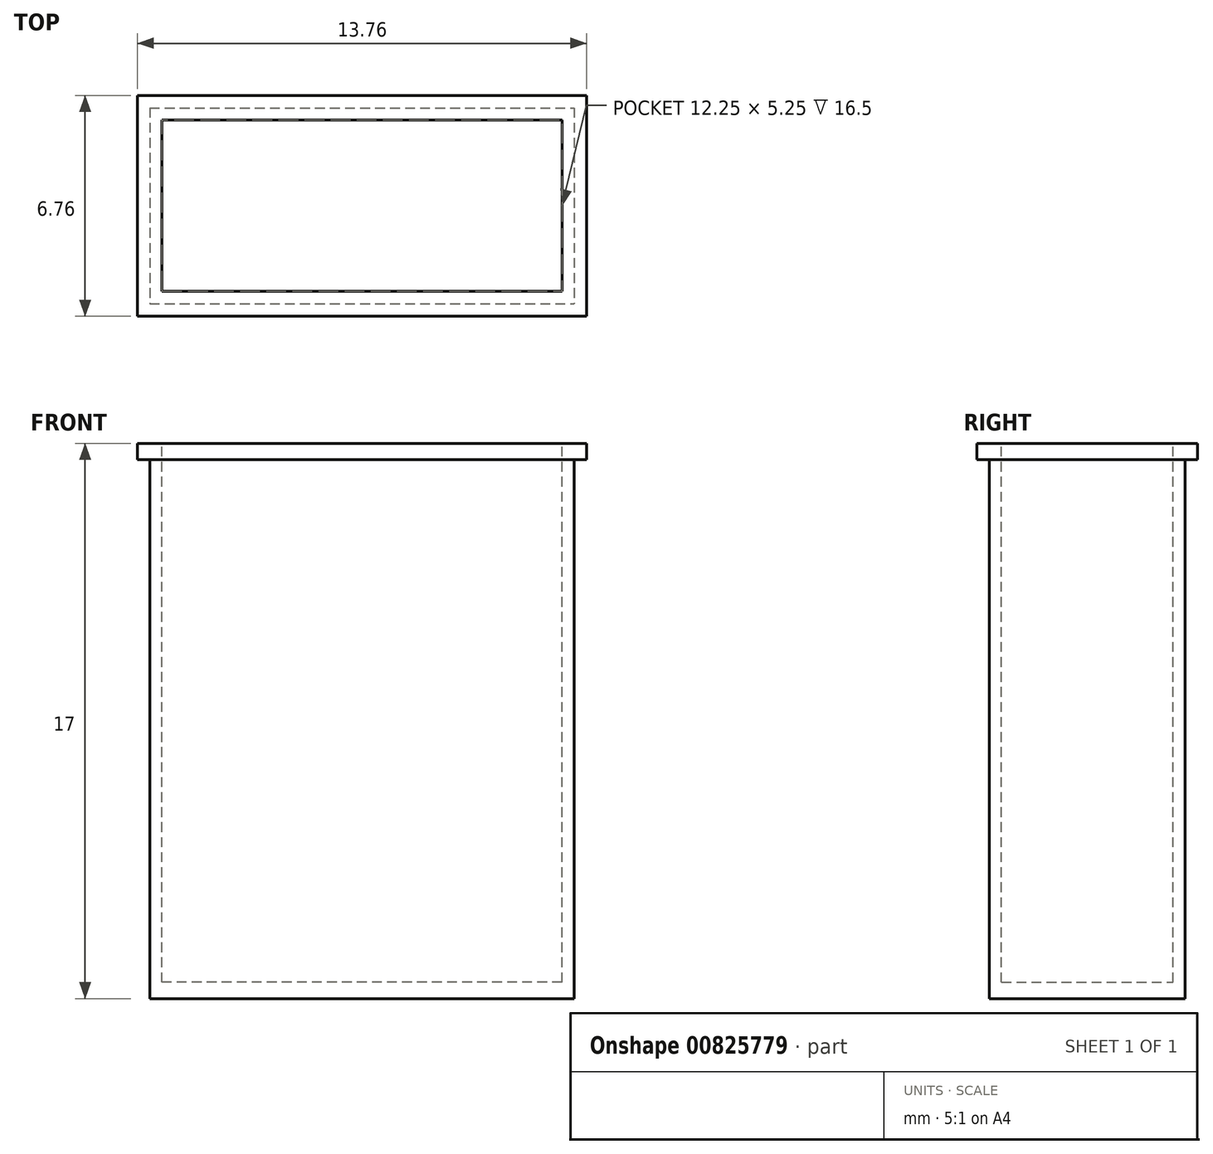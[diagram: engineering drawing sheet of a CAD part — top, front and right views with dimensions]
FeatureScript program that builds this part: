
annotation { "Feature Type Name" : "Feature", "Feature Type Description" : "" }
export const myFeature = defineFeature(function(context is Context, id is Id, definition is map)
    precondition{}
    {
        {
            var Q0;
            Q0=qCreatedBy(makeId("Top.planeOp"),FACE);
            var sketch = newSketch(context, id + "F0", { "sketchPlane" : qUnion([Q0])});
            skLineSegment(sketch, "E0.bottom", {"start": v(-6.5, 3) * mm, "end": v(6.5, 3) * mm});
            skLineSegment(sketch, "E0.top", {"start": v(-6.5, -3) * mm, "end": v(6.5, -3) * mm});
            skLineSegment(sketch, "E0.left", {"start": v(-6.5, 3) * mm, "end": v(-6.5, -3) * mm});
            skLineSegment(sketch, "E0.right", {"start": v(6.5, 3) * mm, "end": v(6.5, -3) * mm});
            skLineSegment(sketch, "E1", {"start": v(0, 0) * mm, "end": v(-6.5, 0) * mm, "construction": true});
            skLineSegment(sketch, "E2", {"start": v(0, 0) * mm, "end": v(0, 3) * mm, "construction": true});
            skLineSegment(sketch, "E3", {"start": v(0, 0) * mm, "end": v(6.5, 0) * mm, "construction": true});
            skLineSegment(sketch, "E4", {"start": v(0, 0) * mm, "end": v(0, -3) * mm, "construction": true});
            skSolve(sketch);
        }
        {
            var Q0;
            Q0=makeQuery(id+"F0.imprint","IMPRINT",FACE,{"disambiguationData":[TD([[makeQuery(id+"F0.imprint","IMPRINT",EDGE,{"derivedFrom":sQuery(id+"F0.wireOp",EDGE,"E0.bottom")}),-1.0]])]});
            extrude(context, id + "F1", {"entities" : qUnion([Q0]), "depth" : 17 * mm, "offsetDistance" : 25 * mm});
        }
        {
            var Q0;
            Q0=makeQuery(id+"F1.opExtrude","CAP_FACE",FACE,{"disambiguationData":[OSD([sQuery(id+"F0.wireOp",EDGE,"E0.bottom"),sQuery(id+"F0.wireOp",EDGE,"E0.top"),sQuery(id+"F0.wireOp",EDGE,"E0.left"),sQuery(id+"F0.wireOp",EDGE,"E0.right")])],"isStart":false});
            var sketch = newSketch(context, id + "F2", { "sketchPlane" : qUnion([Q0])});
            skLineSegment(sketch, "E5.bottom", {"start": v(-6.88, 3.38) * mm, "end": v(6.88, 3.38) * mm});
            skLineSegment(sketch, "E5.top", {"start": v(-6.88, -3.37) * mm, "end": v(6.87, -3.37) * mm});
            skLineSegment(sketch, "E5.left", {"start": v(-6.88, 3.38) * mm, "end": v(-6.88, -3.37) * mm});
            skLineSegment(sketch, "E5.right", {"start": v(6.88, 3.38) * mm, "end": v(6.87, -3.37) * mm});
            skPoint(sketch, "E5.middle", {"position": v(0, 0) * mm});
            skSolve(sketch);
        }
        {
            var Q0;
            Q0=makeQuery(id+"F2.imprint","IMPRINT",FACE,{"disambiguationData":[TD([[makeQuery(id+"F2.imprint","IMPRINT",EDGE,{"derivedFrom":sQuery(id+"F2.wireOp",EDGE,"E5.bottom")}),-1.0]])]});
            var Q1;
            Q1=makeQuery(id+"F2.imprint","IMPRINT",FACE,{"disambiguationData":[TD([[makeQuery(id+"F2.imprint","IMPRINT",EDGE,{"derivedFrom":makeQuery(id+"F1.opExtrude","CAP_EDGE",EDGE,{"disambiguationData":[OSD([sQuery(id+"F0.wireOp",EDGE,"E0.bottom")])],"isStart":false})}),-1.0]])]});
            extrude(context, id + "F3", {"entities" : qUnion([Q0, Q1]), "operationType" : NewBodyOperationType.ADD, "oppositeDirection" : true, "depth" : .5 * mm, "offsetDistance" : 25 * mm});
        }
        {
            var Q0;
            Q0=makeQuery(id+"F3.boolean.opBoolean","MERGE",FACE,{"derivedFrom":[makeQuery(id+"F1.opExtrude","CAP_FACE",FACE,{"disambiguationData":[OSD([sQuery(id+"F0.wireOp",EDGE,"E0.bottom"),sQuery(id+"F0.wireOp",EDGE,"E0.top"),sQuery(id+"F0.wireOp",EDGE,"E0.left"),sQuery(id+"F0.wireOp",EDGE,"E0.right")])],"isStart":false}),makeQuery(id+"F3.opExtrude","CAP_FACE",FACE,{"disambiguationData":[OSD([sQuery(id+"F2.wireOp",EDGE,"E5.bottom"),sQuery(id+"F2.wireOp",EDGE,"E5.top"),sQuery(id+"F2.wireOp",EDGE,"E5.left"),sQuery(id+"F2.wireOp",EDGE,"E5.right")])],"isStart":true})]});
            var sketch = newSketch(context, id + "F4", { "sketchPlane" : qUnion([Q0])});
            skLineSegment(sketch, "E6.bottom", {"start": v(-6.12, 2.63) * mm, "end": v(6.13, 2.63) * mm});
            skLineSegment(sketch, "E6.top", {"start": v(-6.13, -2.62) * mm, "end": v(6.12, -2.62) * mm});
            skLineSegment(sketch, "E6.left", {"start": v(-6.12, 2.63) * mm, "end": v(-6.13, -2.62) * mm});
            skLineSegment(sketch, "E6.right", {"start": v(6.13, 2.63) * mm, "end": v(6.12, -2.62) * mm});
            skPoint(sketch, "E6.middle", {"position": v(0, 0) * mm});
            skSolve(sketch);
        }
        {
            var Q0;
            Q0=makeQuery(id+"F4.imprint","IMPRINT",FACE,{"disambiguationData":[TD([[makeQuery(id+"F4.imprint","IMPRINT",EDGE,{"derivedFrom":sQuery(id+"F4.wireOp",EDGE,"E6.bottom")}),-1.0]])]});
            var Q1;
            Q1=makeQuery(id+"F1.opExtrude","CAP_FACE",FACE,{"disambiguationData":[OSD([sQuery(id+"F0.wireOp",EDGE,"E0.bottom"),sQuery(id+"F0.wireOp",EDGE,"E0.top"),sQuery(id+"F0.wireOp",EDGE,"E0.left"),sQuery(id+"F0.wireOp",EDGE,"E0.right")])],"isStart":true});
            extrude(context, id + "F5", {"entities" : qUnion([Q0]), "operationType" : NewBodyOperationType.REMOVE, "endBound" : BoundingType.UP_TO_SURFACE, "oppositeDirection" : true, "depth" : 5 * mm, "endBoundEntityFace" : qUnion([Q1]), "hasOffset" : true, "offsetDistance" : .5 * mm});
        }
    });
